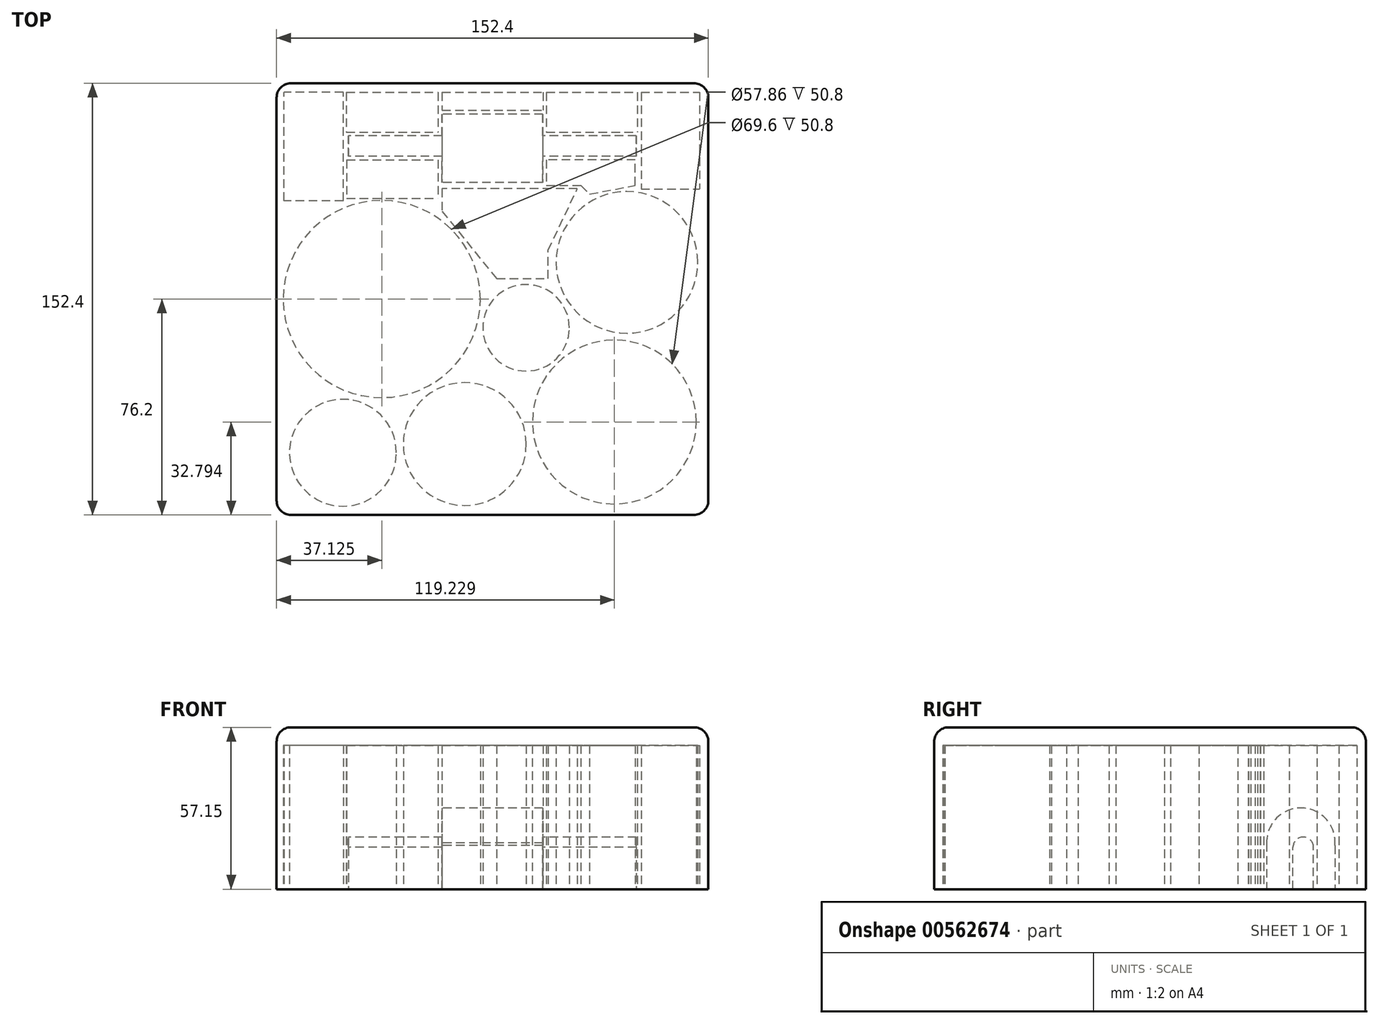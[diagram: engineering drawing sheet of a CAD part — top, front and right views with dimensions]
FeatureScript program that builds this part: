
annotation { "Feature Type Name" : "Feature", "Feature Type Description" : "" }
export const myFeature = defineFeature(function(context is Context, id is Id, definition is map)
    precondition{}
    {
        {
            var Q0;
            Q0=qCreatedBy(makeId("Top.planeOp"),FACE);
            var sketch = newSketch(context, id + "F0", { "sketchPlane" : qUnion([Q0])});
            skLineSegment(sketch, "E0.bottom", {"start": v(76.2, 76.2) * mm, "end": v(-76.2, 76.2) * mm});
            skLineSegment(sketch, "E0.top", {"start": v(76.2, -76.2) * mm, "end": v(-76.2, -76.2) * mm});
            skLineSegment(sketch, "E0.left", {"start": v(76.2, 76.2) * mm, "end": v(76.2, -76.2) * mm});
            skLineSegment(sketch, "E0.right", {"start": v(-76.2, 76.2) * mm, "end": v(-76.2, -76.2) * mm});
            skPoint(sketch, "E0.middle", {"position": v(0, 0) * mm});
            skSolve(sketch);
        }
        {
            var Q0;
            Q0=makeQuery(id+"F0.imprint","IMPRINT",FACE,{"disambiguationData":[TD([[makeQuery(id+"F0.imprint","IMPRINT",EDGE,{"derivedFrom":sQuery(id+"F0.wireOp",EDGE,"E0.bottom")}),1.0]])]});
            extrude(context, id + "F1", {"entities" : qUnion([Q0]), "depth" : 57.15 * mm, "offsetDistance" : 25.4 * mm});
        }
        {
            var Q0;
            Q0=makeQuery(id+"F1.opExtrude","SWEPT_EDGE",EDGE,{"disambiguationData":[OSD([sQuery(id+"F0.wireOp",EDGE,"E0.top"),sQuery(id+"F0.wireOp",EDGE,"E0.right")])]});
            var Q1;
            Q1=makeQuery(id+"F1.opExtrude","SWEPT_EDGE",EDGE,{"disambiguationData":[OSD([sQuery(id+"F0.wireOp",EDGE,"E0.top"),sQuery(id+"F0.wireOp",EDGE,"E0.left")])]});
            var Q2;
            Q2=makeQuery(id+"F1.opExtrude","SWEPT_EDGE",EDGE,{"disambiguationData":[OSD([sQuery(id+"F0.wireOp",EDGE,"E0.bottom"),sQuery(id+"F0.wireOp",EDGE,"E0.left")])]});
            var Q3;
            Q3=makeQuery(id+"F1.opExtrude","SWEPT_EDGE",EDGE,{"disambiguationData":[OSD([sQuery(id+"F0.wireOp",EDGE,"E0.bottom"),sQuery(id+"F0.wireOp",EDGE,"E0.right")])]});
            var Q4;
            Q4=makeQuery(id+"F1.opExtrude","CAP_FACE",FACE,{"disambiguationData":[OSD([sQuery(id+"F0.wireOp",EDGE,"E0.bottom"),sQuery(id+"F0.wireOp",EDGE,"E0.top"),sQuery(id+"F0.wireOp",EDGE,"E0.left"),sQuery(id+"F0.wireOp",EDGE,"E0.right")])],"isStart":false});
            fillet(context, id + "F2", {"entities" : qUnion([Q0, Q1, Q2, Q3, Q4]), "radius" : 5.08 * mm, "tangentPropagation" : true, "allowEdgeOverflow" : false});
        }
        {
            var Q0;
            Q0=qCreatedBy(makeId("Top.planeOp"),FACE);
            var sketch = newSketch(context, id + "F3", { "sketchPlane" : qUnion([Q0])});
            skCircle(sketch, "E1", {"center": v(-52.8, -54.26) * mm, "radius": 18.87 * mm});
            skCircle(sketch, "E2", {"center": v(-9.77, -51.2) * mm, "radius": 21.7 * mm});
            skCircle(sketch, "E3", {"center": v(43.03, -43.4) * mm, "radius": 28.93 * mm});
            skCircle(sketch, "E4", {"center": v(-39.07, 0) * mm, "radius": 34.8 * mm});
            skCircle(sketch, "E5", {"center": v(11.86, -10.14) * mm, "radius": 15.27 * mm});
            skCircle(sketch, "E6", {"center": v(47.45, 12.98) * mm, "radius": 25 * mm});
            skSolve(sketch);
        }
        {
            var Q0;
            Q0 = qSketchRegion(id + "F3", true);
            extrude(context, id + "F4", {"entities" : qUnion([Q0]), "operationType" : NewBodyOperationType.REMOVE, "depth" : 50.8 * mm, "offsetDistance" : 25.4 * mm});
        }
        {
            var Q0;
            Q0=qCreatedBy(makeId("Right.planeOp"),FACE);
            var sketch = newSketch(context, id + "F5", { "sketchPlane" : qUnion([Q0])});
            skCircle(sketch, "E7", {"center": v(53.23, 16.64) * mm, "radius": 12.07 * mm});
            skLineSegment(sketch, "E8.bottom", {"start": v(41.17, 16.98) * mm, "end": v(65.23, 16.98) * mm});
            skLineSegment(sketch, "E8.top", {"start": v(41.17, 0) * mm, "end": v(65.23, 0) * mm});
            skLineSegment(sketch, "E8.left", {"start": v(41.17, 16.98) * mm, "end": v(41.17, 0) * mm});
            skLineSegment(sketch, "E8.right", {"start": v(65.23, 16.98) * mm, "end": v(65.23, 0) * mm});
            skSolve(sketch);
        }
        {
            var Q0;
            Q0 = qSketchRegion(id + "F5", true);
            extrude(context, id + "F6", {"entities" : qUnion([Q0]), "operationType" : NewBodyOperationType.REMOVE, "endBound" : BoundingType.SYMMETRIC, "depth" : 35.56 * mm, "offsetDistance" : 25.4 * mm});
        }
        {
            var Q0;
            Q0=qCreatedBy(makeId("Right.planeOp"),FACE);
            var sketch = newSketch(context, id + "F7", { "sketchPlane" : qUnion([Q0])});
            skCircle(sketch, "E9", {"center": v(54.08, 14.8) * mm, "radius": 3.62 * mm});
            skLineSegment(sketch, "E10.bottom", {"start": v(50.46, 14.86) * mm, "end": v(57.7, 14.86) * mm});
            skLineSegment(sketch, "E10.top", {"start": v(50.46, -1.9) * mm, "end": v(57.7, -1.9) * mm});
            skLineSegment(sketch, "E10.left", {"start": v(50.46, 14.86) * mm, "end": v(50.46, -1.9) * mm});
            skLineSegment(sketch, "E10.right", {"start": v(57.7, 14.86) * mm, "end": v(57.7, -1.9) * mm});
            skSolve(sketch);
        }
        {
            var Q0;
            Q0 = qSketchRegion(id + "F7", true);
            extrude(context, id + "F8", {"entities" : qUnion([Q0]), "operationType" : NewBodyOperationType.REMOVE, "endBound" : BoundingType.SYMMETRIC, "depth" : 101.6 * mm, "offsetDistance" : 25.4 * mm});
        }
        {
            var Q0;
            Q0=qCreatedBy(makeId("Top.planeOp"),FACE);
            var sketch = newSketch(context, id + "F9", { "sketchPlane" : qUnion([Q0])});
            skLineSegment(sketch, "E11.bottom", {"start": v(-52.67, 34.69) * mm, "end": v(-73.64, 34.69) * mm});
            skLineSegment(sketch, "E11.top", {"start": v(-52.67, 73) * mm, "end": v(-73.64, 73) * mm});
            skLineSegment(sketch, "E11.left", {"start": v(-52.67, 34.69) * mm, "end": v(-52.67, 73) * mm});
            skLineSegment(sketch, "E11.right", {"start": v(-73.64, 34.69) * mm, "end": v(-73.64, 73) * mm});
            skLineSegment(sketch, "E12.bottom", {"start": v(-51.56, 73) * mm, "end": v(-19.2, 73) * mm});
            skLineSegment(sketch, "E12.top", {"start": v(-51.56, 58.98) * mm, "end": v(-19.2, 58.98) * mm});
            skLineSegment(sketch, "E12.left", {"start": v(-51.56, 73) * mm, "end": v(-51.56, 58.98) * mm});
            skLineSegment(sketch, "E12.right", {"start": v(-19.2, 73) * mm, "end": v(-19.2, 58.98) * mm});
            skLineSegment(sketch, "E13.bottom", {"start": v(-17.8, 73) * mm, "end": v(17.9, 73) * mm});
            skLineSegment(sketch, "E13.top", {"start": v(-17.8, 66.64) * mm, "end": v(17.9, 66.64) * mm});
            skLineSegment(sketch, "E13.left", {"start": v(-17.8, 73) * mm, "end": v(-17.8, 66.64) * mm});
            skLineSegment(sketch, "E13.right", {"start": v(17.9, 73) * mm, "end": v(17.9, 66.64) * mm});
            skLineSegment(sketch, "E14.bottom", {"start": v(19, 73) * mm, "end": v(51.16, 73) * mm});
            skLineSegment(sketch, "E14.top", {"start": v(19, 58.98) * mm, "end": v(51.16, 58.98) * mm});
            skLineSegment(sketch, "E14.left", {"start": v(19, 73) * mm, "end": v(19, 58.98) * mm});
            skLineSegment(sketch, "E14.right", {"start": v(51.16, 73) * mm, "end": v(51.16, 58.98) * mm});
            skLineSegment(sketch, "E15.bottom", {"start": v(52.48, 73) * mm, "end": v(73.04, 73) * mm});
            skLineSegment(sketch, "E15.top", {"start": v(52.48, 38.82) * mm, "end": v(73.04, 38.82) * mm});
            skLineSegment(sketch, "E15.left", {"start": v(52.48, 73) * mm, "end": v(52.48, 38.82) * mm});
            skLineSegment(sketch, "E15.right", {"start": v(73.04, 73) * mm, "end": v(73.04, 38.82) * mm});
            skSolve(sketch);
        }
        {
            var Q0;
            Q0 = qSketchRegion(id + "F9", true);
            extrude(context, id + "F10", {"entities" : qUnion([Q0]), "operationType" : NewBodyOperationType.REMOVE, "depth" : 50.8 * mm, "offsetDistance" : 25.4 * mm});
        }
        {
            var Q0;
            Q0=qCreatedBy(makeId("Top.planeOp"),FACE);
            var sketch = newSketch(context, id + "F11", { "sketchPlane" : qUnion([Q0])});
            skLineSegment(sketch, "E16", {"start": v(-17.83, 38.96) * mm, "end": v(-17.83, 30.99) * mm});
            skLineSegment(sketch, "E17", {"start": v(-17.83, 30.99) * mm, "end": v(1.5, 7.25) * mm});
            skLineSegment(sketch, "E18", {"start": v(1.5, 7.25) * mm, "end": v(19.64, 7.25) * mm});
            skLineSegment(sketch, "E19", {"start": v(19.64, 7.25) * mm, "end": v(19.64, 17.26) * mm});
            skLineSegment(sketch, "E20", {"start": v(19.64, 17.26) * mm, "end": v(29.98, 38.96) * mm});
            skLineSegment(sketch, "E21", {"start": v(29.98, 38.96) * mm, "end": v(-17.83, 38.96) * mm});
            skSolve(sketch);
        }
        {
            var Q0;
            Q0 = qSketchRegion(id + "F11", true);
            extrude(context, id + "F12", {"entities" : qUnion([Q0]), "operationType" : NewBodyOperationType.REMOVE, "depth" : 50.8 * mm, "offsetDistance" : 25.4 * mm});
        }
        {
            var Q0;
            Q0=qCreatedBy(makeId("Top.planeOp"),FACE);
            var sketch = newSketch(context, id + "F13", { "sketchPlane" : qUnion([Q0])});
            skLineSegment(sketch, "E22.bottom", {"start": v(-51.48, 49.12) * mm, "end": v(-19.27, 49.12) * mm});
            skLineSegment(sketch, "E22.top", {"start": v(-51.48, 35.56) * mm, "end": v(-19.27, 35.56) * mm});
            skLineSegment(sketch, "E22.left", {"start": v(-51.48, 49.12) * mm, "end": v(-51.48, 35.56) * mm});
            skLineSegment(sketch, "E22.right", {"start": v(-19.27, 49.12) * mm, "end": v(-19.27, 35.56) * mm});
            skLineSegment(sketch, "E23", {"start": v(19.05, 49.12) * mm, "end": v(19.05, 40.14) * mm});
            skLineSegment(sketch, "E24", {"start": v(19.05, 40.14) * mm, "end": v(31.26, 40.14) * mm});
            skLineSegment(sketch, "E25", {"start": v(31.26, 40.14) * mm, "end": v(34.3, 37.08) * mm});
            skLineSegment(sketch, "E26", {"start": v(34.3, 37.08) * mm, "end": v(50.42, 40.14) * mm});
            skLineSegment(sketch, "E27", {"start": v(50.42, 40.14) * mm, "end": v(50.42, 49.12) * mm});
            skLineSegment(sketch, "E28", {"start": v(50.42, 49.12) * mm, "end": v(19.05, 49.12) * mm});
            skSolve(sketch);
        }
        {
            var Q0;
            Q0 = qSketchRegion(id + "F13", true);
            extrude(context, id + "F14", {"entities" : qUnion([Q0]), "operationType" : NewBodyOperationType.REMOVE, "depth" : 50.8 * mm, "offsetDistance" : 25.4 * mm});
        }
    });
